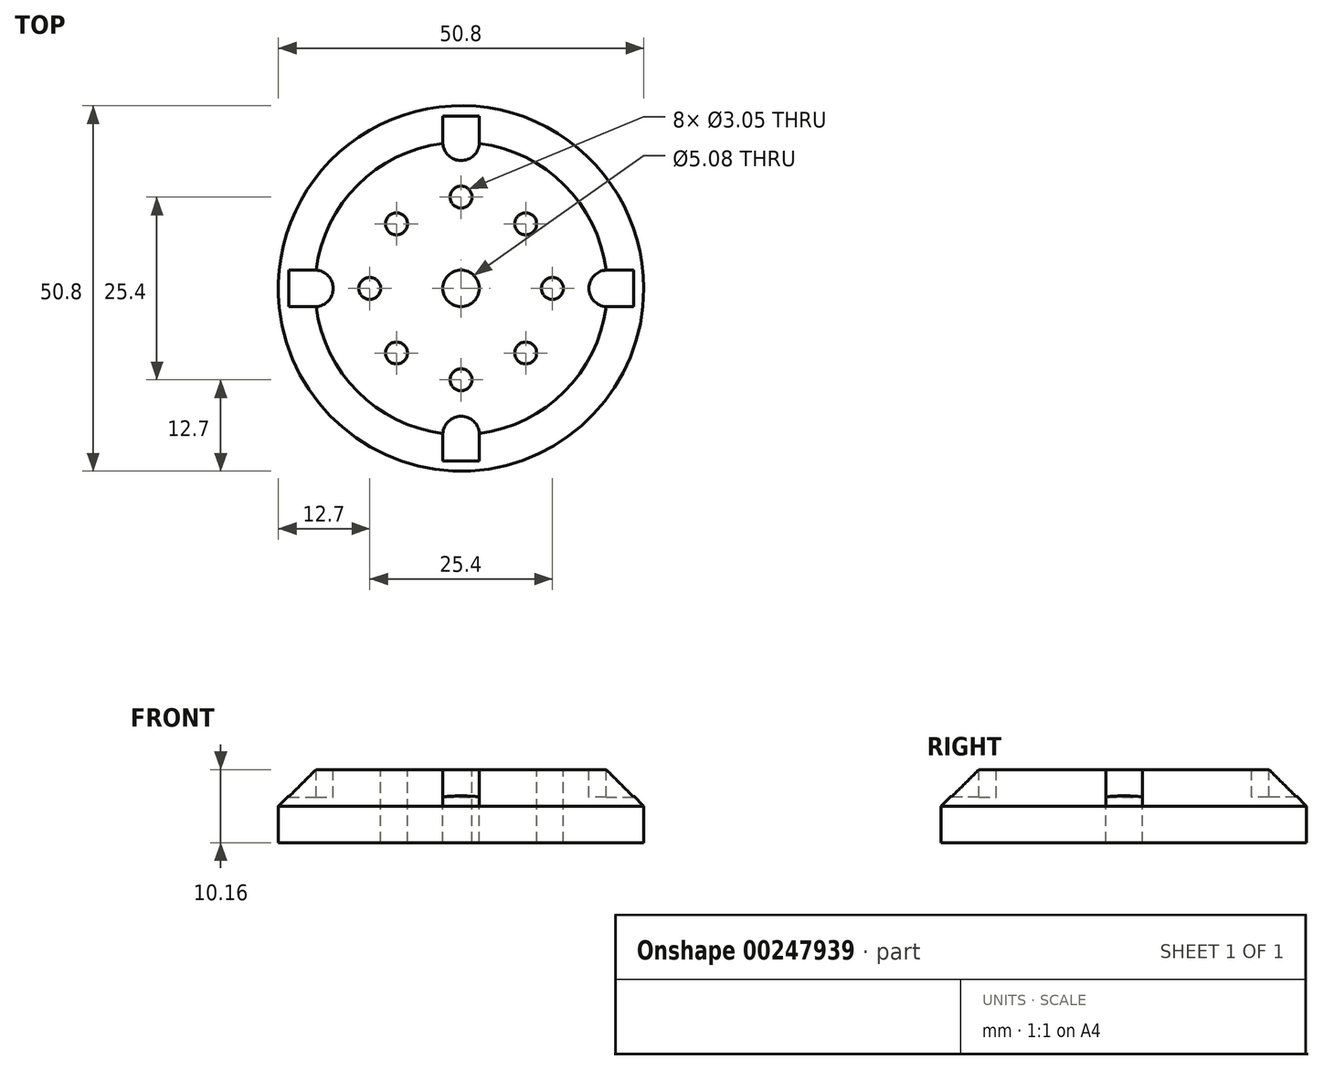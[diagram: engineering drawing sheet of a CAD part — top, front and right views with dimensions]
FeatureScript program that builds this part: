
annotation { "Feature Type Name" : "Feature", "Feature Type Description" : "" }
export const myFeature = defineFeature(function(context is Context, id is Id, definition is map)
    precondition{}
    {
        {
            var Q0;
            Q0=qCreatedBy(makeId("Top.planeOp"),FACE);
            var sketch = newSketch(context, id + "F0", { "sketchPlane" : qUnion([Q0])});
            skCircle(sketch, "E0", {"center": v(0, 0) * mm, "radius": 25.4 * mm});
            skSolve(sketch);
        }
        {
            var Q0;
            Q0=makeQuery(id+"F0.imprint","IMPRINT",FACE,{"disambiguationData":[TD([[makeQuery(id+"F0.imprint","IMPRINT",EDGE,{"derivedFrom":sQuery(id+"F0.wireOp",EDGE,"E0")}),1.0]])]});
            extrude(context, id + "F1", {"entities" : qUnion([Q0]), "depth" : 10.16 * mm});
        }
        {
            var Q0;
            Q0=makeQuery(id+"F1.opExtrude","CAP_EDGE",EDGE,{"disambiguationData":[OSD([sQuery(id+"F0.wireOp",EDGE,"E0")])],"isStart":false});
            chamfer(context, id + "F2", {"entities" : qUnion([Q0]), "width" : 5.08 * mm, "tangentPropagation" : true});
        }
        {
            var Q0;
            Q0=makeQuery(id+"F1.opExtrude","CAP_FACE",FACE,{"disambiguationData":[OSD([sQuery(id+"F0.wireOp",EDGE,"E0")])],"isStart":false});
            var sketch = newSketch(context, id + "F3", { "sketchPlane" : qUnion([Q0])});
            skCircle(sketch, "E1", {"center": v(0, 0) * mm, "radius": 2.54 * mm});
            skSolve(sketch);
        }
        {
            var Q0;
            Q0=makeQuery(id+"F3.imprint","IMPRINT",FACE,{"disambiguationData":[TD([[makeQuery(id+"F3.imprint","IMPRINT",EDGE,{"derivedFrom":sQuery(id+"F3.wireOp",EDGE,"E1")}),1.0]])]});
            extrude(context, id + "F4", {"entities" : qUnion([Q0]), "operationType" : NewBodyOperationType.REMOVE, "endBound" : BoundingType.THROUGH_ALL, "oppositeDirection" : true, "depth" : 25.4 * mm});
        }
        {
            var Q0;
            Q0=makeQuery(id+"F1.opExtrude","CAP_FACE",FACE,{"disambiguationData":[OSD([sQuery(id+"F0.wireOp",EDGE,"E0")])],"isStart":false});
            var sketch = newSketch(context, id + "F5", { "sketchPlane" : qUnion([Q0])});
            skCircle(sketch, "E2", {"center": v(0, 0) * mm, "radius": 12.7 * mm, "construction": true});
            skCircle(sketch, "E3", {"center": v(0, 12.7) * mm, "radius": 1.52 * mm});
            skCircle(sketch, "E4.1.0", {"center": v(-8.98, 8.98) * mm, "radius": 1.52 * mm});
            skCircle(sketch, "E4.2.0", {"center": v(-12.7, 0) * mm, "radius": 1.52 * mm});
            skCircle(sketch, "E4.3.0", {"center": v(-8.98, -8.98) * mm, "radius": 1.52 * mm});
            skCircle(sketch, "E4.4.0", {"center": v(0, -12.7) * mm, "radius": 1.52 * mm});
            skCircle(sketch, "E4.5.0", {"center": v(8.98, -8.98) * mm, "radius": 1.52 * mm});
            skCircle(sketch, "E4.6.0", {"center": v(12.7, 0) * mm, "radius": 1.52 * mm});
            skCircle(sketch, "E4.7.0", {"center": v(8.98, 8.98) * mm, "radius": 1.52 * mm});
            skSolve(sketch);
        }
        {
            var Q0;
            Q0=makeQuery(id+"F5.imprint","IMPRINT",FACE,{"disambiguationData":[TD([[makeQuery(id+"F5.imprint","IMPRINT",EDGE,{"derivedFrom":sQuery(id+"F5.wireOp",EDGE,"E4.3.0")}),1.0]])]});
            var Q1;
            Q1=makeQuery(id+"F5.imprint","IMPRINT",FACE,{"disambiguationData":[TD([[makeQuery(id+"F5.imprint","IMPRINT",EDGE,{"derivedFrom":sQuery(id+"F5.wireOp",EDGE,"E4.5.0")}),1.0]])]});
            var Q2;
            Q2=makeQuery(id+"F5.imprint","IMPRINT",FACE,{"disambiguationData":[TD([[makeQuery(id+"F5.imprint","IMPRINT",EDGE,{"derivedFrom":sQuery(id+"F5.wireOp",EDGE,"E3")}),1.0]])]});
            var Q3;
            Q3=makeQuery(id+"F5.imprint","IMPRINT",FACE,{"disambiguationData":[TD([[makeQuery(id+"F5.imprint","IMPRINT",EDGE,{"derivedFrom":sQuery(id+"F5.wireOp",EDGE,"E4.1.0")}),1.0]])]});
            var Q4;
            Q4=makeQuery(id+"F5.imprint","IMPRINT",FACE,{"disambiguationData":[TD([[makeQuery(id+"F5.imprint","IMPRINT",EDGE,{"derivedFrom":sQuery(id+"F5.wireOp",EDGE,"E4.2.0")}),1.0]])]});
            var Q5;
            Q5=makeQuery(id+"F5.imprint","IMPRINT",FACE,{"disambiguationData":[TD([[makeQuery(id+"F5.imprint","IMPRINT",EDGE,{"derivedFrom":sQuery(id+"F5.wireOp",EDGE,"E4.6.0")}),1.0]])]});
            var Q6;
            Q6=makeQuery(id+"F5.imprint","IMPRINT",FACE,{"disambiguationData":[TD([[makeQuery(id+"F5.imprint","IMPRINT",EDGE,{"derivedFrom":sQuery(id+"F5.wireOp",EDGE,"E4.7.0")}),1.0]])]});
            var Q7;
            Q7=makeQuery(id+"F5.imprint","IMPRINT",FACE,{"disambiguationData":[TD([[makeQuery(id+"F5.imprint","IMPRINT",EDGE,{"derivedFrom":sQuery(id+"F5.wireOp",EDGE,"E4.4.0")}),1.0]])]});
            extrude(context, id + "F6", {"entities" : qUnion([Q0, Q1, Q2, Q3, Q4, Q5, Q6, Q7]), "operationType" : NewBodyOperationType.REMOVE, "endBound" : BoundingType.THROUGH_ALL, "oppositeDirection" : true, "depth" : 25.4 * mm});
        }
        {
            var Q0;
            Q0=makeQuery(id+"F1.opExtrude","CAP_FACE",FACE,{"disambiguationData":[OSD([sQuery(id+"F0.wireOp",EDGE,"E0")])],"isStart":false});
            var sketch = newSketch(context, id + "F7", { "sketchPlane" : qUnion([Q0])});
            skLineSegment(sketch, "E5", {"start": v(0, 20.32) * mm, "end": v(0, -20.32) * mm, "construction": true});
            skLineSegment(sketch, "E6", {"start": v(-20.32, 0) * mm, "end": v(20.32, 0) * mm, "construction": true});
            skArc(sketch, "E7", {"start": v(20.16, 2.54) * mm, "mid": v(17.78, 0) * mm, "end": v(20.16, -2.54) * mm});
            skLineSegment(sketch, "E8", {"start": v(20.16, -2.54) * mm, "end": v(23.97, -2.54) * mm});
            skLineSegment(sketch, "E9", {"start": v(23.97, -2.54) * mm, "end": v(23.97, 2.54) * mm});
            skLineSegment(sketch, "E10", {"start": v(23.97, 2.54) * mm, "end": v(20.16, 2.54) * mm});
            skArc(sketch, "E11.1.0", {"start": v(2.54, -20.16) * mm, "mid": v(0, -17.78) * mm, "end": v(-2.54, -20.16) * mm});
            skLineSegment(sketch, "E11.1.1", {"start": v(2.54, -23.97) * mm, "end": v(2.54, -20.16) * mm});
            skLineSegment(sketch, "E11.1.2", {"start": v(-2.54, -23.97) * mm, "end": v(2.54, -23.97) * mm});
            skLineSegment(sketch, "E11.1.3", {"start": v(-2.54, -20.16) * mm, "end": v(-2.54, -23.97) * mm});
            skArc(sketch, "E11.2.0", {"start": v(-20.16, -2.54) * mm, "mid": v(-17.78, 0) * mm, "end": v(-20.16, 2.54) * mm});
            skLineSegment(sketch, "E11.2.1", {"start": v(-23.97, -2.54) * mm, "end": v(-20.16, -2.54) * mm});
            skLineSegment(sketch, "E11.2.2", {"start": v(-23.97, 2.54) * mm, "end": v(-23.97, -2.54) * mm});
            skLineSegment(sketch, "E11.2.3", {"start": v(-20.16, 2.54) * mm, "end": v(-23.97, 2.54) * mm});
            skArc(sketch, "E11.3.0", {"start": v(-2.54, 20.16) * mm, "mid": v(0, 17.78) * mm, "end": v(2.54, 20.16) * mm});
            skLineSegment(sketch, "E11.3.1", {"start": v(-2.54, 23.97) * mm, "end": v(-2.54, 20.16) * mm});
            skLineSegment(sketch, "E11.3.2", {"start": v(2.54, 23.97) * mm, "end": v(-2.54, 23.97) * mm});
            skLineSegment(sketch, "E11.3.3", {"start": v(2.54, 20.16) * mm, "end": v(2.54, 23.97) * mm});
            skPoint(sketch, "E11.center", {"position": v(0, 0) * mm});
            skLineSegment(sketch, "E11.anchor1", {"start": v(0, 0) * mm, "end": v(20.16, -2.54) * mm, "construction": true});
            skLineSegment(sketch, "E11.anchor2", {"start": v(0, 0) * mm, "end": v(2.54, 20.16) * mm, "construction": true});
            skSolve(sketch);
        }
        {
            var Q0;
            {var subQ0=sQuery(id+"F7.wireOp",EDGE,"E8");Q0=makeQuery(id+"F7.imprint","IMPRINT",FACE,{"disambiguationData":[TD([[makeQuery(id+"F7.imprint","IMPRINT",EDGE,{"derivedFrom":subQ0}),1.0]])]});}
            var Q1;
            {var subQ0=sQuery(id+"F7.wireOp",EDGE,"E7");Q1=makeQuery(id+"F7.imprint","IMPRINT",FACE,{"disambiguationData":[TD([[makeQuery(id+"F7.imprint","IMPRINT",EDGE,{"derivedFrom":subQ0}),1.0]])]});}
            var Q2;
            {var subQ0=sQuery(id+"F7.wireOp",EDGE,"E11.3.1");Q2=makeQuery(id+"F7.imprint","IMPRINT",FACE,{"disambiguationData":[TD([[makeQuery(id+"F7.imprint","IMPRINT",EDGE,{"derivedFrom":subQ0}),1.0]])]});}
            var Q3;
            {var subQ0=sQuery(id+"F7.wireOp",EDGE,"E11.3.0");Q3=makeQuery(id+"F7.imprint","IMPRINT",FACE,{"disambiguationData":[TD([[makeQuery(id+"F7.imprint","IMPRINT",EDGE,{"derivedFrom":subQ0}),1.0]])]});}
            var Q4;
            {var subQ0=sQuery(id+"F7.wireOp",EDGE,"E11.2.1");Q4=makeQuery(id+"F7.imprint","IMPRINT",FACE,{"disambiguationData":[TD([[makeQuery(id+"F7.imprint","IMPRINT",EDGE,{"derivedFrom":subQ0}),1.0]])]});}
            var Q5;
            {var subQ0=sQuery(id+"F7.wireOp",EDGE,"E11.2.0");Q5=makeQuery(id+"F7.imprint","IMPRINT",FACE,{"disambiguationData":[TD([[makeQuery(id+"F7.imprint","IMPRINT",EDGE,{"derivedFrom":subQ0}),1.0]])]});}
            var Q6;
            {var subQ0=sQuery(id+"F7.wireOp",EDGE,"E11.1.0");Q6=makeQuery(id+"F7.imprint","IMPRINT",FACE,{"disambiguationData":[TD([[makeQuery(id+"F7.imprint","IMPRINT",EDGE,{"derivedFrom":subQ0}),1.0]])]});}
            var Q7;
            {var subQ0=sQuery(id+"F7.wireOp",EDGE,"E11.1.1");Q7=makeQuery(id+"F7.imprint","IMPRINT",FACE,{"disambiguationData":[TD([[makeQuery(id+"F7.imprint","IMPRINT",EDGE,{"derivedFrom":subQ0}),1.0]])]});}
            extrude(context, id + "F8", {"entities" : qUnion([Q0, Q1, Q2, Q3, Q4, Q5, Q6, Q7]), "operationType" : NewBodyOperationType.REMOVE, "oppositeDirection" : true, "depth" : 3.8 * mm});
        }
    });
